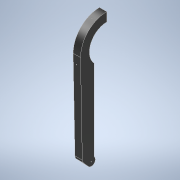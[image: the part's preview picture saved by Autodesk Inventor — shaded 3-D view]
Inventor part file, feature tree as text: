
AUTODESK INVENTOR PART (.ipt)
format: ipt  version: 2021 (Build 250183000, 183)  size: 1,105,408 bytes
history: native  units: mm
features: other x10, sketch x5, extrude x3, hole x2, plane x1, reference x1
ambient origin geometry x8: Origin, YZ Plane, XZ Plane, XY Plane, X Axis, Y Axis, Z Axis, Center Point
bodies: Body1 (feature_tree), Body2 (feature_tree)
feature tree (22):
  other  "Sólido1"
  extrude  "Extrusión1"  Depth=4.0mm
  other  "Superficie reglada1"
  other  "Engrosado1"
  other  "Punto de trabajo1"
  extrude  "Extrusión2"  Depth=34.0mm TaperAngle=0.0deg
  hole  "Agujero1"  [1 undecoded]
  hole  "Agujero2"  [1 undecoded]
  plane  "Plano de trabajo1"
  extrude  "Extrusión3"  [1 undecoded]
  sketch  "Boceto1"  dims[d1=2100.0mm d6=4.0mm]
  other  "Imagen1"
  other  "Sup1"
  other  "Eje de trabajo1"
  sketch  "Boceto2"  dims[d9=3.0mm d10=0.0mm d11=34.0mm d12=0.0mm]
  sketch  "Boceto3"  dims[d13=3.0mm d14=3.0mm]
  sketch  "Boceto4"  dims[d15=0.0mm d16=0.0mm]
  sketch  "Boceto5"  dims[d17=3.4mm d18=6.0mm d19=4.0mm d20=2.0mm d21=90.0deg d22=8.0mm d23=0.0mm d24=3.4mm d25=6.0mm d26=4.0mm d27=2.0mm d28=90.0deg d29=8.0mm d30=0.0mm d32=0.0mm d33=0.0mm]
  reference  "Referencia1"
  parser-record x1  (decoder bookkeeping rows leaked as tree rows — omitted from the tree; the rows remain in map.json)
  other  "ensamble_general.iam"
  other  "platina_2:1"
note: 3 required parameter values undecoded (feature->parameter linkage not recoverable at this tier; creation-order binding heuristic only, values carry confidence <= 0.55)
note: 1 file-system path scrubbed to <path> (originals preserved in map.json)
